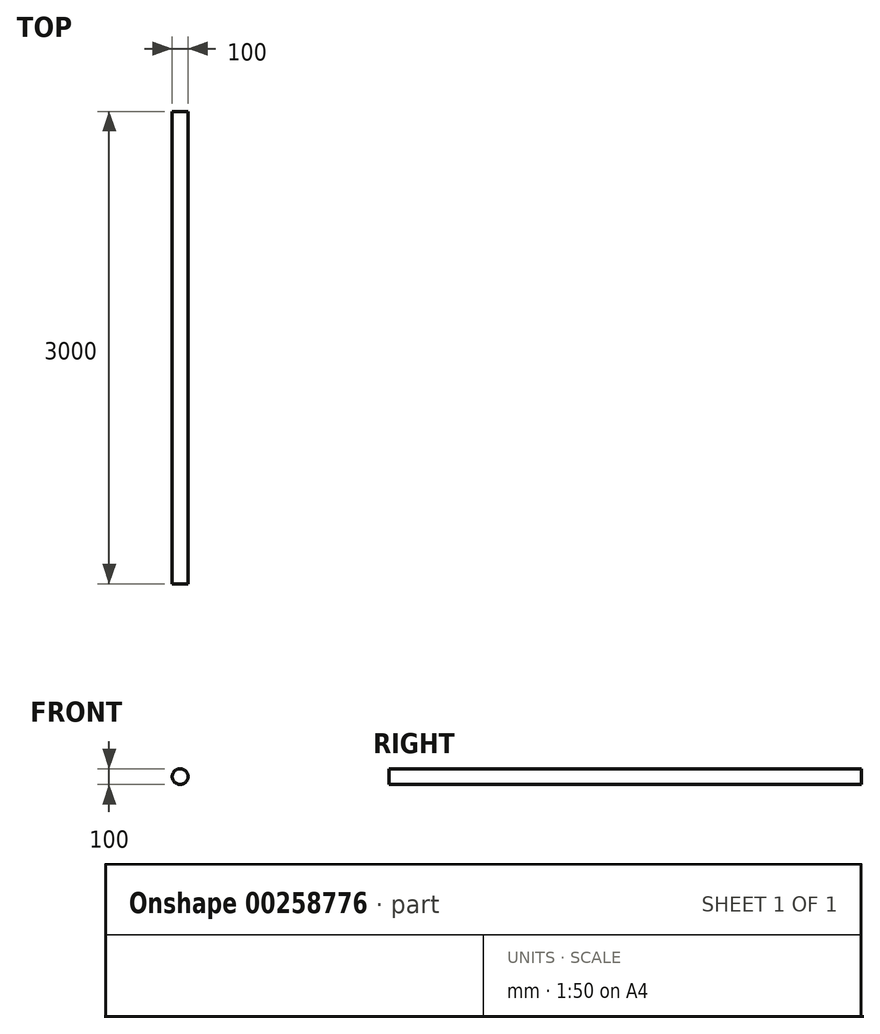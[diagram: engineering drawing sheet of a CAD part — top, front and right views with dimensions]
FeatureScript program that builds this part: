
annotation { "Feature Type Name" : "Feature", "Feature Type Description" : "" }
export const myFeature = defineFeature(function(context is Context, id is Id, definition is map)
    precondition{}
    {
        {
            var Q0;
            Q0=qCreatedBy(makeId("Front.planeOp"),FACE);
            var sketch = newSketch(context, id + "F0", { "sketchPlane" : qUnion([Q0])});
            skCircle(sketch, "E0", {"center": v(0, 0) * mm, "radius": 50 * mm});
            skSolve(sketch);
        }
        {
            var Q0;
            Q0=makeQuery(id+"F0.imprint","IMPRINT",FACE,{"disambiguationData":[TD([[makeQuery(id+"F0.imprint","IMPRINT",EDGE,{"derivedFrom":sQuery(id+"F0.wireOp",EDGE,"E0")}),1.0]])]});
            extrude(context, id + "F1", {"entities" : qUnion([Q0]), "depth" : 3000 * mm});
        }
    });
